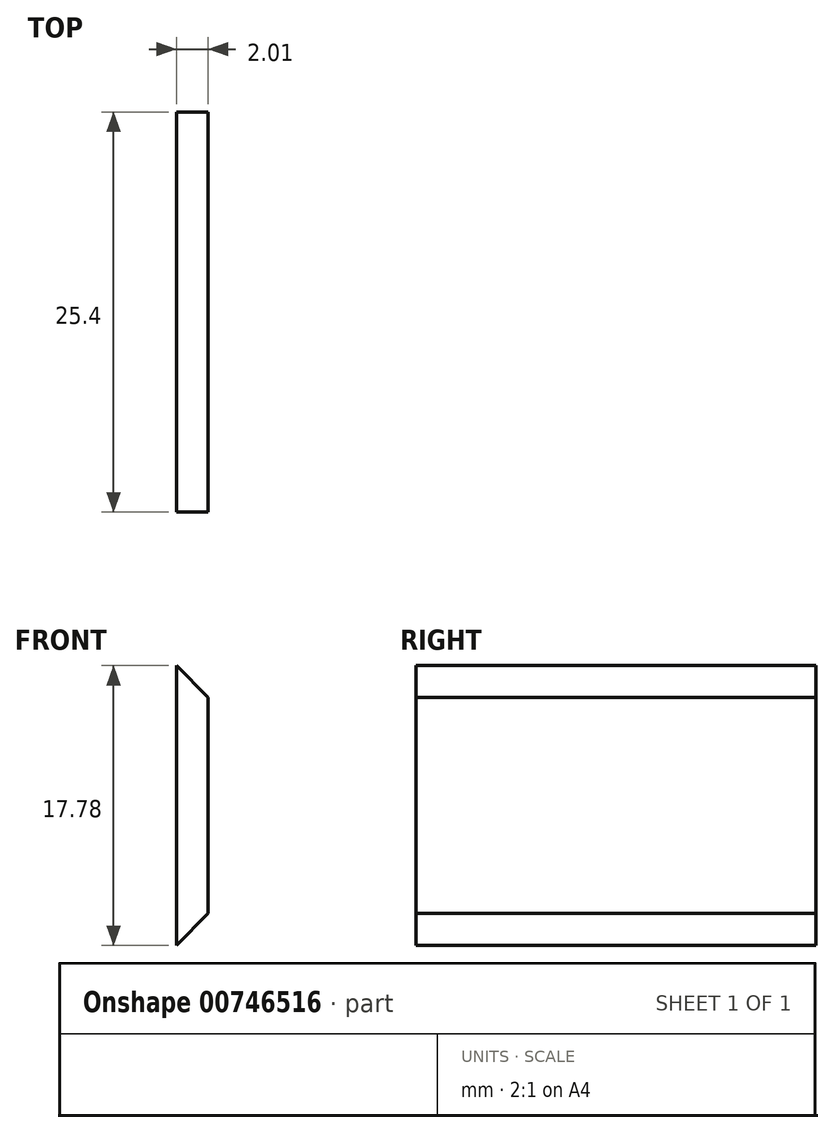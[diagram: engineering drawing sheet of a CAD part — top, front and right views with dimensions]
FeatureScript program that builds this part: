
annotation { "Feature Type Name" : "Feature", "Feature Type Description" : "" }
export const myFeature = defineFeature(function(context is Context, id is Id, definition is map)
    precondition{}
    {
        {
            var Q0;
            Q0=qCreatedBy(makeId("Front.planeOp"),FACE);
            var sketch = newSketch(context, id + "F0", { "sketchPlane" : qUnion([Q0])});
            skLineSegment(sketch, "E0.bottom", {"start": v(-13.7, 11.22) * mm, "end": v(-15.7, 11.22) * mm});
            skLineSegment(sketch, "E0.top", {"start": v(-13.7, 18.11) * mm, "end": v(-15.7, 18.11) * mm});
            skLineSegment(sketch, "E0.left", {"start": v(-13.7, 11.22) * mm, "end": v(-13.7, 18.11) * mm});
            skLineSegment(sketch, "E0.right", {"start": v(-15.7, 11.22) * mm, "end": v(-15.7, 18.11) * mm});
            skSolve(sketch);
        }
        {
            var Q0;
            Q0=makeQuery(id+"F0.imprint","IMPRINT",FACE,{"disambiguationData":[TD([[makeQuery(id+"F0.imprint","IMPRINT",EDGE,{"derivedFrom":sQuery(id+"F0.wireOp",EDGE,"E0.bottom")}),-1.0]])]});
            extrude(context, id + "F1", {"entities" : qUnion([Q0]), "depth" : 25.4 * mm, "offsetDistance" : 25.4 * mm});
        }
        {
            var Q0;
            Q0=makeQuery(id+"F1.opExtrude","CAP_FACE",FACE,{"disambiguationData":[OSD([sQuery(id+"F0.wireOp",EDGE,"E0.bottom"),sQuery(id+"F0.wireOp",EDGE,"E0.top"),sQuery(id+"F0.wireOp",EDGE,"E0.left"),sQuery(id+"F0.wireOp",EDGE,"E0.right")])],"isStart":false});
            var sketch = newSketch(context, id + "F2", { "sketchPlane" : qUnion([Q0])});
            skLineSegment(sketch, "E1.bottom", {"start": v(-15.7, 18.11) * mm, "end": v(-13.7, 18.11) * mm});
            skLineSegment(sketch, "E1.top", {"start": v(-15.7, 24.93) * mm, "end": v(-13.7, 24.93) * mm});
            skLineSegment(sketch, "E1.left", {"start": v(-15.7, 18.11) * mm, "end": v(-15.7, 24.93) * mm});
            skLineSegment(sketch, "E1.right", {"start": v(-13.7, 18.11) * mm, "end": v(-13.7, 24.93) * mm});
            skSolve(sketch);
        }
        {
            var Q0;
            Q0=makeQuery(id+"F2.imprint","IMPRINT",FACE,{"disambiguationData":[TD([[makeQuery(id+"F2.imprint","IMPRINT",EDGE,{"derivedFrom":sQuery(id+"F2.wireOp",EDGE,"E1.bottom")}),-1.0]])]});
            extrude(context, id + "F3", {"entities" : qUnion([Q0]), "operationType" : NewBodyOperationType.ADD, "oppositeDirection" : true, "depth" : 25.4 * mm, "offsetDistance" : 25.4 * mm});
        }
        {
            var Q0;
            Q0=makeQuery(id+"F3.boolean.opBoolean","MERGE",FACE,{"derivedFrom":[makeQuery(id+"F1.opExtrude","CAP_FACE",FACE,{"disambiguationData":[OSD([sQuery(id+"F0.wireOp",EDGE,"E0.bottom"),sQuery(id+"F0.wireOp",EDGE,"E0.top"),sQuery(id+"F0.wireOp",EDGE,"E0.left"),sQuery(id+"F0.wireOp",EDGE,"E0.right")])],"isStart":false}),makeQuery(id+"F3.opExtrude","CAP_FACE",FACE,{"disambiguationData":[OSD([sQuery(id+"F2.wireOp",EDGE,"E1.bottom"),sQuery(id+"F2.wireOp",EDGE,"E1.top"),sQuery(id+"F2.wireOp",EDGE,"E1.left"),sQuery(id+"F2.wireOp",EDGE,"E1.right")])],"isStart":true})]});
            var sketch = newSketch(context, id + "F4", { "sketchPlane" : qUnion([Q0])});
            skLineSegment(sketch, "E2", {"start": v(-15.7, 24.93) * mm, "end": v(-15.7, 26.96) * mm});
            skLineSegment(sketch, "E3", {"start": v(-15.7, 26.96) * mm, "end": v(-13.7, 24.93) * mm});
            skLineSegment(sketch, "E4", {"start": v(-15.7, 11.22) * mm, "end": v(-15.7, 9.18) * mm});
            skLineSegment(sketch, "E5", {"start": v(-15.7, 9.18) * mm, "end": v(-13.7, 11.22) * mm});
            skSolve(sketch);
        }
        {
            var Q0;
            Q0=makeQuery(id+"F4.imprint","IMPRINT",FACE,{"disambiguationData":[TD([[makeQuery(id+"F4.imprint","IMPRINT",EDGE,{"derivedFrom":sQuery(id+"F4.wireOp",EDGE,"E2")}),-1.0]])]});
            var Q1;
            Q1=makeQuery(id+"F4.imprint","IMPRINT",FACE,{"disambiguationData":[TD([[makeQuery(id+"F4.imprint","IMPRINT",EDGE,{"derivedFrom":sQuery(id+"F4.wireOp",EDGE,"E4")}),1.0]])]});
            extrude(context, id + "F5", {"entities" : qUnion([Q0, Q1]), "operationType" : NewBodyOperationType.ADD, "oppositeDirection" : true, "depth" : 25.4 * mm, "offsetDistance" : 25.4 * mm});
        }
    });
